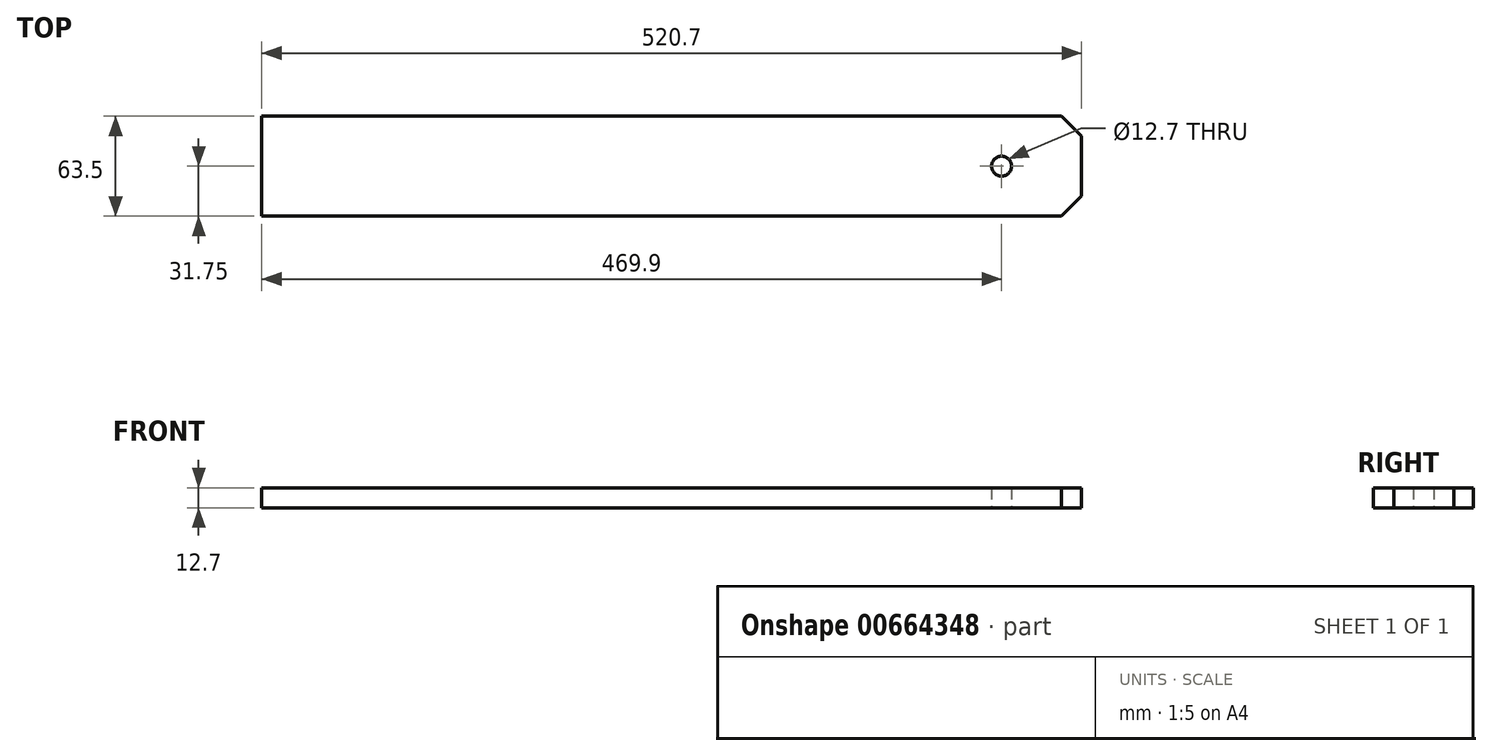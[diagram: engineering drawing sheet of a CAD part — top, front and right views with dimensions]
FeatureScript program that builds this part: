
annotation { "Feature Type Name" : "Feature", "Feature Type Description" : "" }
export const myFeature = defineFeature(function(context is Context, id is Id, definition is map)
    precondition{}
    {
        {
            var Q0;
            Q0=qCreatedBy(makeId("Top.planeOp"),FACE);
            var sketch = newSketch(context, id + "F0", { "sketchPlane" : qUnion([Q0])});
            skLineSegment(sketch, "E0", {"start": v(-469.9, 31.75) * mm, "end": v(50.8, 31.75) * mm});
            skLineSegment(sketch, "E1", {"start": v(50.8, 31.75) * mm, "end": v(50.8, -31.75) * mm});
            skLineSegment(sketch, "E2", {"start": v(50.8, -31.75) * mm, "end": v(-469.9, -31.75) * mm});
            skLineSegment(sketch, "E3", {"start": v(-469.9, -31.75) * mm, "end": v(-469.9, 31.75) * mm});
            skLineSegment(sketch, "E4", {"start": v(0, 0) * mm, "end": v(-469.9, 0) * mm, "construction": true});
            skCircle(sketch, "E5", {"center": v(0, 0) * mm, "radius": 6.35 * mm});
            skSolve(sketch);
        }
        {
            var Q0;
            Q0 = qSketchRegion(id + "F0", true);
            extrude(context, id + "F1", {"entities" : qUnion([Q0]), "depth" : 12.7 * mm, "offsetDistance" : 25.4 * mm});
        }
        {
            var Q0;
            Q0=makeQuery(id+"F1.opExtrude","SWEPT_EDGE",EDGE,{"disambiguationData":[OSD([sQuery(id+"F0.wireOp",EDGE,"E1"),sQuery(id+"F0.wireOp",EDGE,"E2")])]});
            var Q1;
            Q1=makeQuery(id+"F1.opExtrude","SWEPT_EDGE",EDGE,{"disambiguationData":[OSD([sQuery(id+"F0.wireOp",EDGE,"E0"),sQuery(id+"F0.wireOp",EDGE,"E1")])]});
            chamfer(context, id + "F2", {"entities" : qUnion([Q0, Q1]), "width" : 12.7 * mm, "tangentPropagation" : true});
        }
    });
